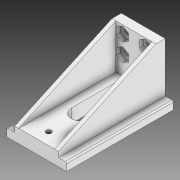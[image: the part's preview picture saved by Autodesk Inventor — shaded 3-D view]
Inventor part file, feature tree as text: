
AUTODESK INVENTOR PART (.ipt)
format: ipt  version: 2020 (Build 240168000, 168)  size: 278,016 bytes
history: native  units: mm
features: extrude x9, sketch x9, fillet x1
ambient origin geometry x8: Origin, YZ Plane, XZ Plane, XY Plane, X Axis, Y Axis, Z Axis, Center Point
bodies: Solid1 (feature_tree)
feature tree (19):
  extrude  "Extrusion1"  Depth=43.4mm
  extrude  "Extrusion2"  Depth=6.0mm
  extrude  "Extrusion3"  Depth=6.0mm
  extrude  "Extrusion4"  Depth=5.0mm
  extrude  "Extrusion5"  Depth=7.0mm TaperAngle=0.0deg
  extrude  "Extrusion6"  Depth=73.0mm TaperAngle=0.0deg
  extrude  "Extrusion7"  TaperAngle=120.0deg  [1 undecoded]
  extrude  "Extrusion8"  Depth=9.0mm TaperAngle=120.0deg
  extrude  "Extrusion10"  Depth=9.0mm TaperAngle=120.0deg
  fillet  "Fillet1"  Radius=3.0mm
  sketch  "Sketch1"  dims[d0=27.0mm d1=43.4mm]
  sketch  "Sketch2"  dims[d2=4.0mm d3=6.0mm]
  sketch  "Sketch3"  dims[d4=6.0mm d5=5.0mm]
  sketch  "Sketch4"  dims[d6=5.0mm d7=5.0mm]
  sketch  "Sketch5"  dims[d8=5.0mm d11=7.0mm d12=0.0mm]
  sketch  "Sketch6"  dims[d13=10.0mm d14=73.0mm d15=0.0mm]
  sketch  "Sketch7"  dims[d16=120.0deg d17=120.0deg]
  sketch  "Sketch8"  dims[d18=9.0mm d19=120.0deg d20=120.0deg d21=9.0mm]
  sketch  "Sketch10"  dims[d22=120.0deg d23=120.0deg d24=9.0mm d25=120.0deg d26=120.0deg d27=9.0mm d28=3.0mm d29=0.0mm d30=3.0mm d31=0.0mm d32=3.0mm d33=0.0mm d34=4.0mm d35=13.5mm d37=74.0mm d38=0.0mm d39=33.0mm d40=14.0mm d41=9.5mm d42=47.0mm d43=10.0mm d44=0.0mm d45=71.0mm d49=74.0mm d50=0.0mm d56=6.0mm d57=6.0mm d58=74.0mm d59=0.0mm d60=1.0mm d61=13.49mm d62=13.49mm]
note: 1 required parameter value undecoded (feature->parameter linkage not recoverable at this tier; creation-order binding heuristic only, values carry confidence <= 0.55)
